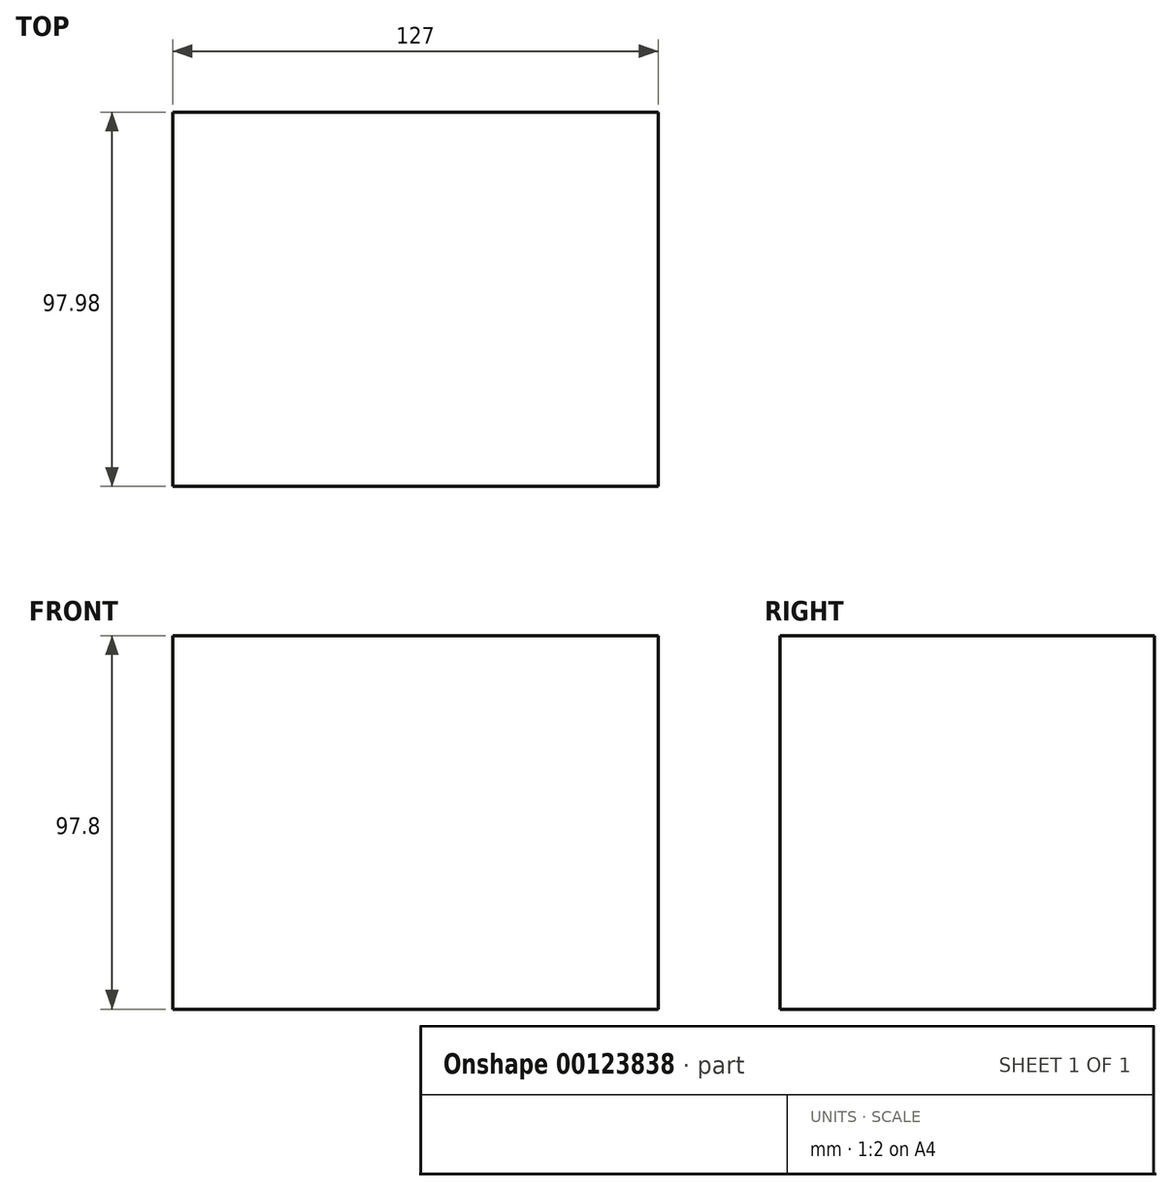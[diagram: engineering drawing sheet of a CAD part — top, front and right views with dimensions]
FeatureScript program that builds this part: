
annotation { "Feature Type Name" : "Feature", "Feature Type Description" : "" }
export const myFeature = defineFeature(function(context is Context, id is Id, definition is map)
    precondition{}
    {
        {
            var Q0;
            Q0=qCreatedBy(makeId("Right.planeOp"),FACE);
            var sketch = newSketch(context, id + "F0", { "sketchPlane" : qUnion([Q0])});
            skLineSegment(sketch, "E0.bottom", {"start": v(-54.5, 53.95) * mm, "end": v(43.49, 53.95) * mm});
            skLineSegment(sketch, "E0.top", {"start": v(-54.5, -43.85) * mm, "end": v(43.49, -43.85) * mm});
            skLineSegment(sketch, "E0.left", {"start": v(-54.5, 53.95) * mm, "end": v(-54.5, -43.85) * mm});
            skLineSegment(sketch, "E0.right", {"start": v(43.49, 53.95) * mm, "end": v(43.49, -43.85) * mm});
            skSolve(sketch);
        }
        {
            var Q0;
            Q0 = qSketchRegion(id + "F0", true);
            extrude(context, id + "F1", {"entities" : qUnion([Q0]), "depth" : 127 * mm});
        }
    });
